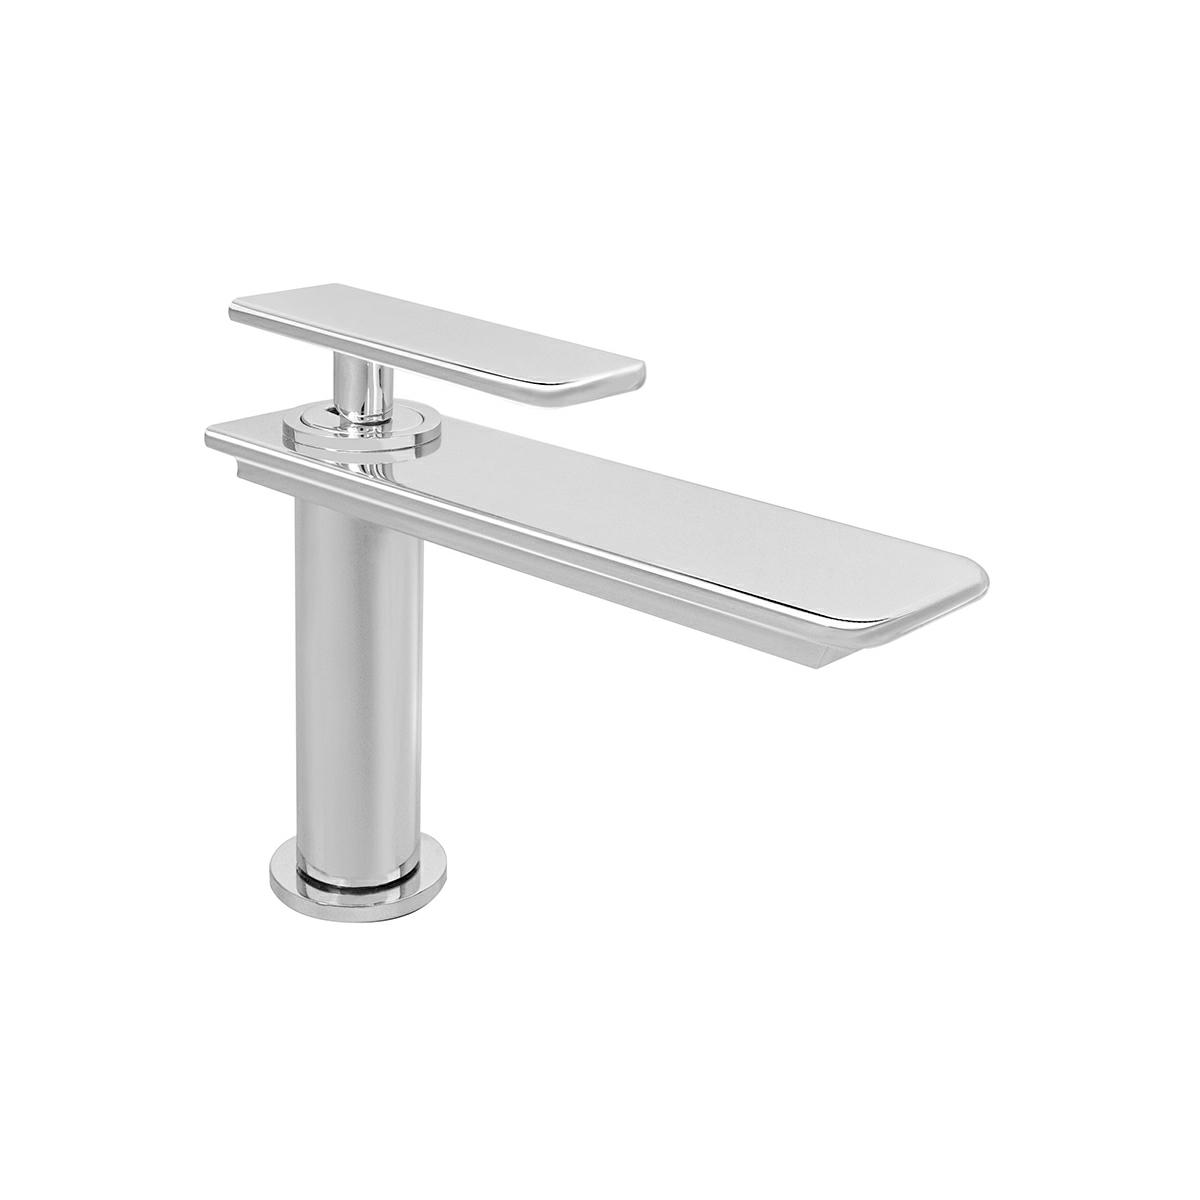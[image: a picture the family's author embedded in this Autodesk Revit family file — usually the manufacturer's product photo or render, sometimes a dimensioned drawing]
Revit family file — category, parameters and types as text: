
# Revit family: E-941
name_source: partatom
category: Aparatos sanitarios
revit_build: Autodesk Revit 2016 (Build: 20150220_1215(x64)
units: mm (PartAtom-declared; Revit-internal decimal feet)

## family parameters
Compartido = Sí
Corte con vacíos al cargar = No
Cota de conector redondo = Diámetro de uso
Número OmniClass = 23.45.55.14
Punto de cálculo de habitación = Sí
Se basa en plano de trabajo = Sí
Siempre vertical = Sí
Tipo de pieza = Normal
Título OmniClass = Single Faucets

## types (1)
- E-941
    Accesorios = Conectores ½ -14 NPSM
    Características del Producto = Monomando para lavabo con contra de push.
    Comentarios de tipo = Monomando para lavabo con contra de push.
    Cuerpo de Latón = Brass
    Descripción = Monomando para lavabo con contra de push.
    Elevación por defecto = 1"
    Fabricante = HELVEX S.A. de C.V.
    Garantía = El producto HELVEX está garantizado como libre de defectos en materiales y procesos de fabricación. El producto HELVEX está garantizado, en lo que se refiere a los acabados; por un periodo de 10 años en los acabados cromo y duravex, y por 2 años en acabados diferentes al cromo, a partir de la fecha de compra indicada en la factura
    Imagen de tipo = E-941.jpg
    Instalación = Conexión ½ - 14 NPSM
    Modelo = E-941
    Operación = El maneral tienen una rotación horizontal para la función de agua caliente y fría; y vertical para abrir y cerrar el flujo de agua.
    Presión Máxima de Trabajo = 85.3 psi
    Presión Mínima de Trabajo = 8.5 psi
    Total Depth = 8"
    Total Height = 6"
    Total Width = 2"

## geometry (parser evidence)
native form markers: Sweep x3
no freeform markers — native parametric forms only
